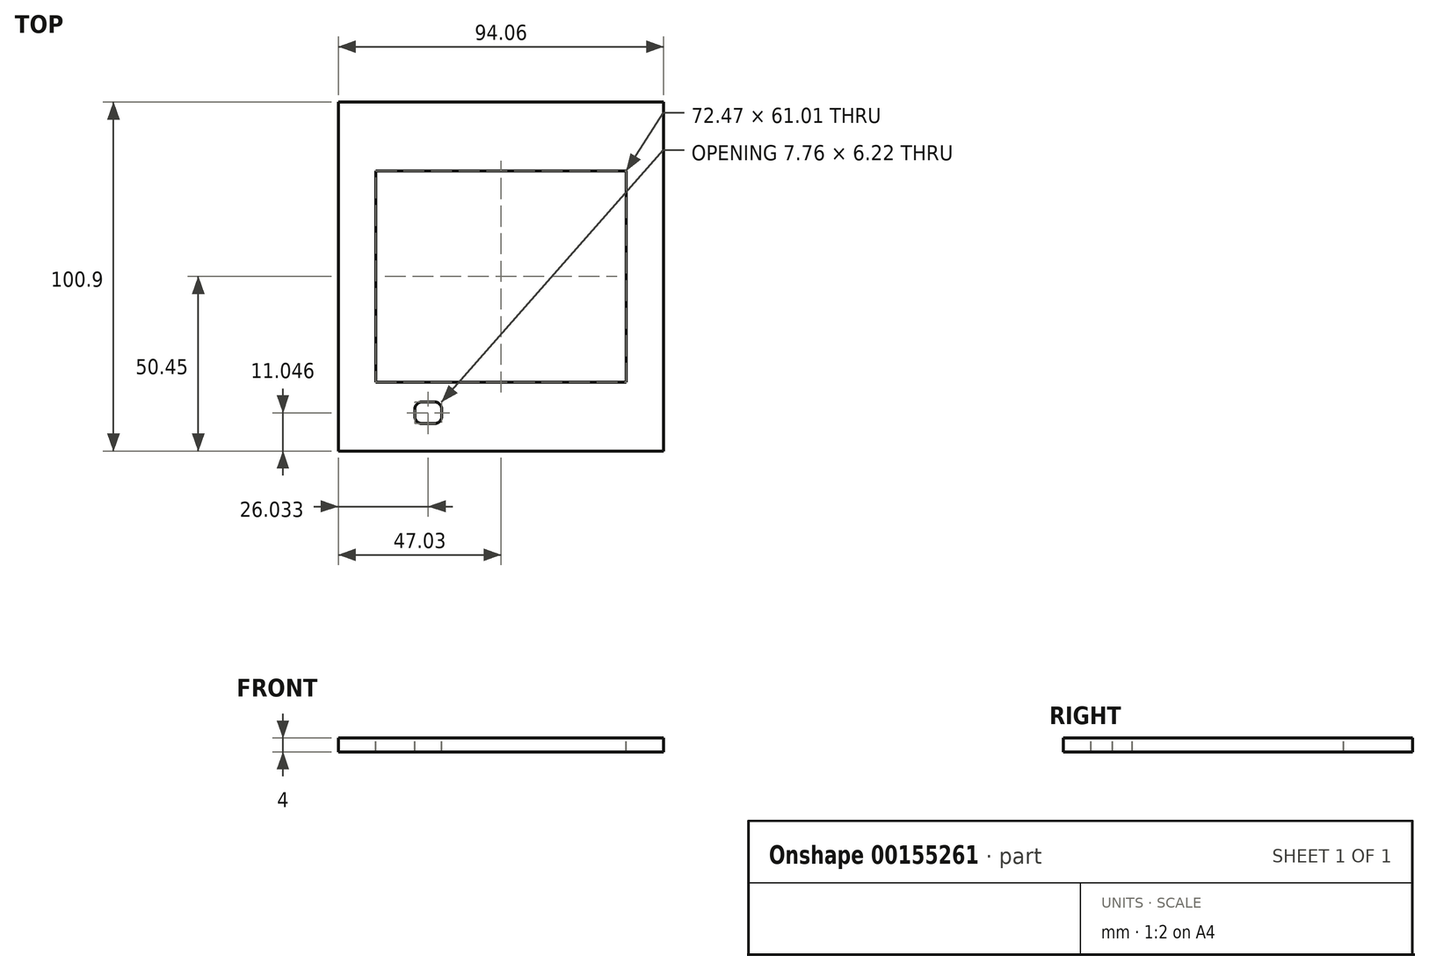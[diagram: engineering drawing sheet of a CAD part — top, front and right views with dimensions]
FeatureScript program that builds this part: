
annotation { "Feature Type Name" : "Feature", "Feature Type Description" : "" }
export const myFeature = defineFeature(function(context is Context, id is Id, definition is map)
    precondition{}
    {
        {
            var Q0;
            Q0=qCreatedBy(makeId("Top.planeOp"),FACE);
            var sketch = newSketch(context, id + "F0", { "sketchPlane" : qUnion([Q0])});
            skLineSegment(sketch, "E0.bottom", {"start": v(47.03, 50.45) * mm, "end": v(-47.03, 50.45) * mm});
            skLineSegment(sketch, "E0.top", {"start": v(47.03, -50.45) * mm, "end": v(-47.03, -50.45) * mm});
            skLineSegment(sketch, "E0.left", {"start": v(47.03, 50.45) * mm, "end": v(47.03, -50.45) * mm});
            skLineSegment(sketch, "E0.right", {"start": v(-47.03, 50.45) * mm, "end": v(-47.03, -50.45) * mm});
            skPoint(sketch, "E0.middle", {"position": v(0, 0) * mm});
            skSolve(sketch);
        }
        {
            var Q0;
            Q0=makeQuery(id+"F0.imprint","IMPRINT",FACE,{"disambiguationData":[TD([[makeQuery(id+"F0.imprint","IMPRINT",EDGE,{"derivedFrom":sQuery(id+"F0.wireOp",EDGE,"E0.bottom")}),1.0]])]});
            extrude(context, id + "F1", {"entities" : qUnion([Q0]), "depth" : 4 * mm});
        }
        {
            var Q0;
            Q0=makeQuery(id+"F1.opExtrude","CAP_FACE",FACE,{"disambiguationData":[OSD([sQuery(id+"F0.wireOp",EDGE,"E0.bottom"),sQuery(id+"F0.wireOp",EDGE,"E0.top"),sQuery(id+"F0.wireOp",EDGE,"E0.left"),sQuery(id+"F0.wireOp",EDGE,"E0.right")])],"isStart":false});
            var sketch = newSketch(context, id + "F6", { "sketchPlane" : qUnion([Q0])});
            skLineSegment(sketch, "E1.bottom", {"start": v(-36.23, 30.5) * mm, "end": v(36.23, 30.5) * mm});
            skLineSegment(sketch, "E1.top", {"start": v(-36.23, -30.5) * mm, "end": v(36.23, -30.5) * mm});
            skLineSegment(sketch, "E1.left", {"start": v(-36.23, 30.5) * mm, "end": v(-36.23, -30.5) * mm});
            skLineSegment(sketch, "E1.right", {"start": v(36.23, 30.5) * mm, "end": v(36.23, -30.5) * mm});
            skPoint(sketch, "E1.middle", {"position": v(0, 0) * mm});
            skSolve(sketch);
        }
        {
            var Q0;
            Q0=makeQuery(id+"F6.imprint","IMPRINT",FACE,{"disambiguationData":[TD([[makeQuery(id+"F6.imprint","IMPRINT",EDGE,{"derivedFrom":sQuery(id+"F6.wireOp",EDGE,"E1.bottom")}),-1.0]])]});
            extrude(context, id + "F2", {"entities" : qUnion([Q0]), "operationType" : NewBodyOperationType.REMOVE, "oppositeDirection" : true, "depth" : 25 * mm});
        }
        {
            var Q0;
            Q0=makeQuery(id+"F1.opExtrude","CAP_FACE",FACE,{"disambiguationData":[OSD([sQuery(id+"F0.wireOp",EDGE,"E0.bottom"),sQuery(id+"F0.wireOp",EDGE,"E0.top"),sQuery(id+"F0.wireOp",EDGE,"E0.left"),sQuery(id+"F0.wireOp",EDGE,"E0.right")])],"isStart":false});
            var sketch = newSketch(context, id + "F3", { "sketchPlane" : qUnion([Q0])});
            skLineSegment(sketch, "E2.bottom", {"start": v(-17.12, -36.3) * mm, "end": v(-24.88, -36.3) * mm});
            skLineSegment(sketch, "E2.top", {"start": v(-17.12, -42.51) * mm, "end": v(-24.88, -42.51) * mm});
            skLineSegment(sketch, "E2.left", {"start": v(-17.12, -36.3) * mm, "end": v(-17.12, -42.51) * mm});
            skLineSegment(sketch, "E2.right", {"start": v(-24.88, -36.3) * mm, "end": v(-24.88, -42.51) * mm});
            skPoint(sketch, "E2.middle", {"position": v(-21, -39.4) * mm});
            skSolve(sketch);
        }
        {
            var Q0;
            Q0=makeQuery(id+"F3.imprint","IMPRINT",FACE,{"disambiguationData":[TD([[makeQuery(id+"F3.imprint","IMPRINT",EDGE,{"derivedFrom":sQuery(id+"F3.wireOp",EDGE,"E2.bottom")}),1.0]])]});
            extrude(context, id + "F4", {"entities" : qUnion([Q0]), "operationType" : NewBodyOperationType.REMOVE, "oppositeDirection" : true, "depth" : 25 * mm});
        }
        {
            var Q0;
            Q0=makeQuery(id+"F4.boolean.opBoolean","COPY",EDGE,{"derivedFrom":makeQuery(id+"F4.opExtrude","SWEPT_EDGE",EDGE,{"disambiguationData":[OSD([sQuery(id+"F3.wireOp",EDGE,"E2.bottom"),sQuery(id+"F3.wireOp",EDGE,"E2.right")])]})});
            var Q1;
            Q1=makeQuery(id+"F4.boolean.opBoolean","COPY",EDGE,{"derivedFrom":makeQuery(id+"F4.opExtrude","SWEPT_EDGE",EDGE,{"disambiguationData":[OSD([sQuery(id+"F3.wireOp",EDGE,"E2.top"),sQuery(id+"F3.wireOp",EDGE,"E2.right")])]})});
            var Q2;
            Q2=makeQuery(id+"F4.boolean.opBoolean","COPY",EDGE,{"derivedFrom":makeQuery(id+"F4.opExtrude","SWEPT_EDGE",EDGE,{"disambiguationData":[OSD([sQuery(id+"F3.wireOp",EDGE,"E2.top"),sQuery(id+"F3.wireOp",EDGE,"E2.left")])]})});
            var Q3;
            Q3=makeQuery(id+"F4.boolean.opBoolean","COPY",EDGE,{"derivedFrom":makeQuery(id+"F4.opExtrude","SWEPT_EDGE",EDGE,{"disambiguationData":[OSD([sQuery(id+"F3.wireOp",EDGE,"E2.bottom"),sQuery(id+"F3.wireOp",EDGE,"E2.left")])]})});
            fillet(context, id + "F5", {"entities" : qUnion([Q0, Q1, Q2, Q3]), "radius" : 2 * mm, "tangentPropagation" : true, "allowEdgeOverflow" : false});
        }
    });
